# Revit family: Legrand_Lighting_Management_KNX_Presence_Sensor_Ceiling
name_source: partatom
category: Dispositifs d'éclairage
units: mm (PartAtom-declared; Revit-internal decimal feet)

## family parameters
Conserver l'orientation des annotations = Non
Cote de connecteur circulaire = Utiliser le diamètre
Couper avec des vides une fois chargée = Non
Hôte = Face
Partagée = Non
Point de calcul de pièce = Non
Type d'élément = Normal

## types (3) — shared parameters
Alarm function = Non
Collecteur de terre = Non
Colour = White
Constant light control = Oui
Cosses d'artère secondaire = Non
Detection angle horizontal (MAX) (°) = 360
Dim function with dimmer basic element = Non
Elévation par défaut = 1219 mm
Fabricant = Legrand
Forced switch off = Non
General Conditions of Use = https://export.legrand.com
HVAC-control = Non
Liaison neutre = Non
Maximum mounting height (m) = 2.5
Min. switch-on time (s) = 5
RAL-number (akin) = 9003
Remote operation = Non
Response value luminosity adjustable = Oui
Response value sensitivity adjustable = Oui
Substation input = Non
Suitable for wireless transmission = Non
URL = http://www.legrandoc.com
zero-valued in all types: Frequency (MAX) (Hz), Frequency (MIN) (Hz), Max. starting current (A), Max. switching power (W), Nominal voltage (V), Response value luminosity (MAX) (lx), Response value luminosity (MIN) (lx), Temperature (MAX) (°C), Temperature (MIN) (°C)

## per-type parameters (varying)
| type | Description | Detection angle horizontal (MIN) (°) | Diameter detection range on floor (m) | Dual-tech KNX faux-plafond 360° | KNX PIR High density | Max. duty cycle (mn) | Max. transmission range frontally (m) | Max. transmission range sideways (m) | Model | Modèle | Mounting method | PIR KNX faux-plafond 2x180° |
| PIR KNX false-ceiling 270°+180° | BUS/KNX motion sensor - ceiling mounted - IP 20 - 360° IR - side range 2 x 12 m | 0 | 3 | Non | Non | 18 | 0 | 12 | Movement sensor | 048919 | Flush mounted (plaster) | Oui |
| KNX PIR High density | BUS/KNX presence sensor - ceiling mounted -IP20 -360° IR + high density lens -8m | 360 | 8 | Non | Oui | 1080 | 4 | 4 | Presence detector | 048922 | Surface mounted (plaster) | Non |
| Dual-tech KNX false-ceiling 360° | BUS/KNX presence sensor - ceiling mounted - IP 20 - 360° IR and ultrasound - 8 m | 0 | 8 | Oui | Non | 18 | 0 | 4 | Movement sensor | 048918 | Flush mounted (plaster) | Non |
